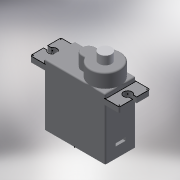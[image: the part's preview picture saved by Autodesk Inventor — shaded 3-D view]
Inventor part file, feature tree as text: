
AUTODESK INVENTOR PART (.ipt)
format: ipt  version: 2017 (Build 210142000, 142)  size: 265,728 bytes
history: native  units: mm
features: sketch x7, extrude x5, other x2, projected_geometry x2, fillet x1
ambient origin geometry x8: Origin, YZ Plane, XZ Plane, XY Plane, X Axis, Y Axis, Z Axis, Center Point
bodies: Body1 (feature_tree)
feature tree (17):
  other  "솔리드1"
  extrude  "돌출1"  Depth=11.0mm
  other  "작업 평면1"
  extrude  "돌출2"  [1 undecoded]
  extrude  "돌출3"  Depth=5.0mm
  fillet  "모깎기1"  Radius=5.0mm
  extrude  "돌출4"  Depth=3.0mm
  extrude  "돌출6"  Depth=1.0mm
  sketch  "Sketch7"  dims[d0=22.0mm d1=11.0mm]
  sketch  "Sketch8"  dims[d2=22.0mm d3=0.0mm d4=-18.5mm d5=5.0mm d6=5.0mm d7=3.0mm d8=2.5mm d9=1.5mm d10=2.0mm d11=0.0mm d12=6.0mm d13=5.0mm d14=5.0mm d15=0.0mm d16=0.5mm d17=4.5mm d18=3.0mm d19=0.0mm d25=1.2mm d26=3.6mm d27=5.0mm d28=1.0mm d29=0.0mm]
  sketch  "스케치1"
  sketch  "스케치2"
  sketch  "스케치3"
  sketch  "스케치4"
  sketch  "스케치6"
  projected_geometry  "Projected Loop1"
  projected_geometry  "Projected Loop2"
note: 1 required parameter value undecoded (feature->parameter linkage not recoverable at this tier; creation-order binding heuristic only, values carry confidence <= 0.55)
